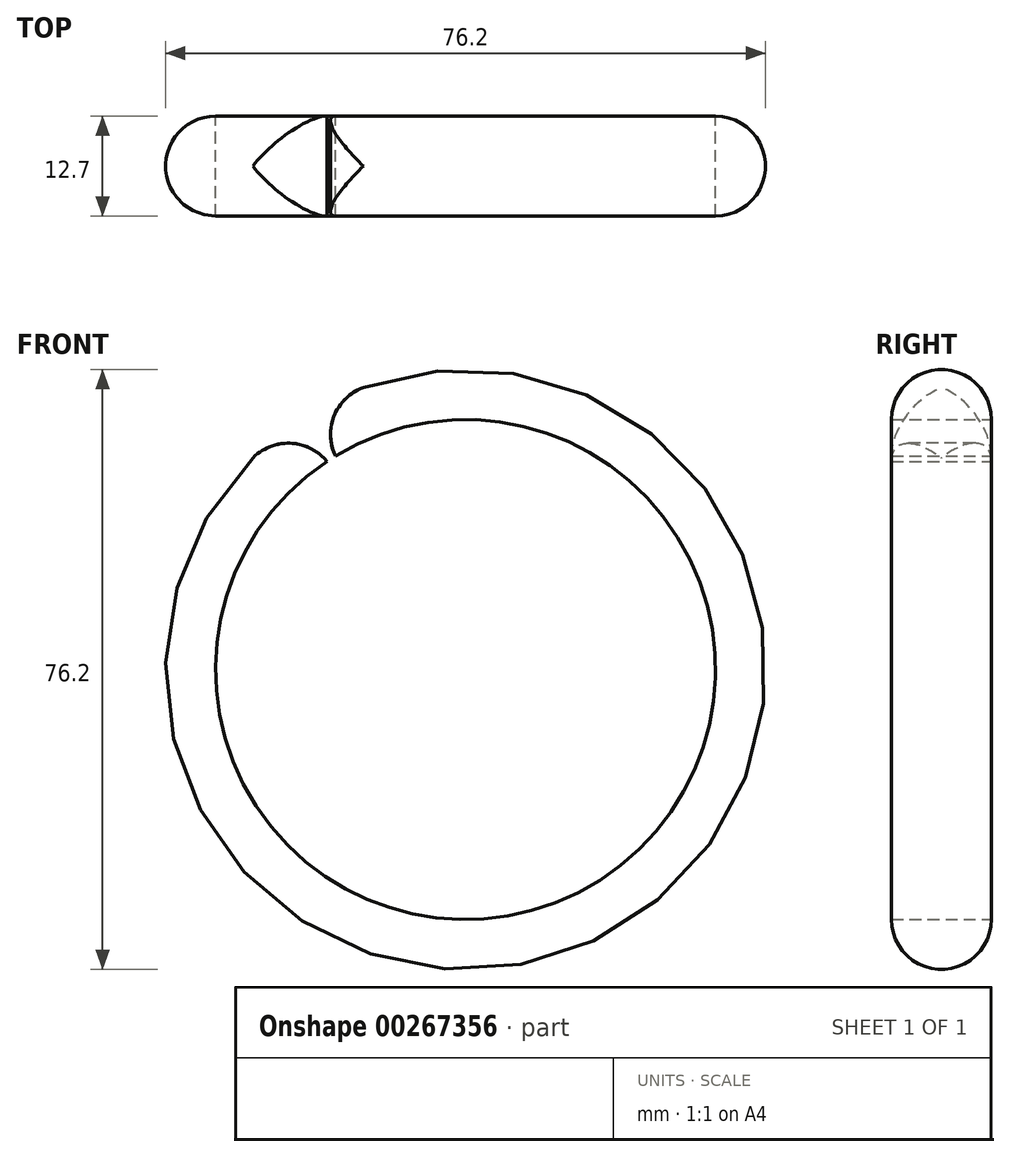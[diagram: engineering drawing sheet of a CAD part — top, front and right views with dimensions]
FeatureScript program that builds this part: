
annotation { "Feature Type Name" : "Feature", "Feature Type Description" : "" }
export const myFeature = defineFeature(function(context is Context, id is Id, definition is map)
    precondition{}
    {
        {
            var Q0;
            Q0=qCreatedBy(makeId("Front.planeOp"),FACE);
            var sketch = newSketch(context, id + "F0", { "sketchPlane" : qUnion([Q0])});
            skArc(sketch, "E0", {"start": v(-21.01, 31.78) * mm, "mid": v(20.48, -32.13) * mm, "end": v(-19.94, 32.47) * mm});
            skLineSegment(sketch, "E1", {"start": v(-21.01, 31.78) * mm, "end": v(-17.6, 26.43) * mm});
            skArc(sketch, "E2.0", {"start": v(-17.6, 26.43) * mm, "mid": v(17.06, -26.77) * mm, "end": v(-16.53, 27.11) * mm});
            skLineSegment(sketch, "E3.trimOffspring", {"start": v(-16.53, 27.11) * mm, "end": v(-19.94, 32.47) * mm});
            skSolve(sketch);
        }
        {
            var Q0;
            Q0 = qSketchRegion(id + "F0", true);
            extrude(context, id + "F1", {"entities" : qUnion([Q0]), "endBound" : BoundingType.SYMMETRIC, "depth" : 12.7 * mm});
        }
        {
            var Q0;
            Q0=makeQuery(id+"F1.opExtrude","SWEPT_EDGE",EDGE,{"disambiguationData":[OSD([sQuery(id+"F0.wireOp",EDGE,"E0"),sQuery(id+"F0.wireOp",EDGE,"E1")])]});
            var Q1;
            Q1=makeQuery(id+"F1.opExtrude","SWEPT_EDGE",EDGE,{"disambiguationData":[OSD([sQuery(id+"F0.wireOp",EDGE,"E0"),sQuery(id+"F0.wireOp",EDGE,"E3.trimOffspring")])]});
            var Q2;
            Q2=makeQuery(id+"F1.opExtrude","CAP_EDGE",EDGE,{"disambiguationData":[OSD([sQuery(id+"F0.wireOp",EDGE,"E0")])],"isStart":false});
            var Q3;
            Q3=makeQuery(id+"F1.opExtrude","CAP_EDGE",EDGE,{"disambiguationData":[OSD([sQuery(id+"F0.wireOp",EDGE,"E0")])],"isStart":true});
            fillet(context, id + "F2", {"entities" : qUnion([Q0, Q1, Q2, Q3]), "radius" : 6.35 * mm, "tangentPropagation" : true, "allowEdgeOverflow" : false});
        }
    });
